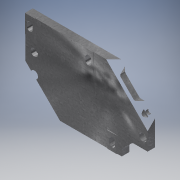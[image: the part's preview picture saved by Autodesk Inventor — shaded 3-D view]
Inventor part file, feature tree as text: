
AUTODESK INVENTOR PART (.ipt)
format: ipt  version: 2016 Beta3 (Build 200134000, 134) ContinuousBuild 0  size: 233,984 bytes
history: native  units: in
note: dims shown in document units (in); Inventor stores cm internally (conversion verified against a paired STEP export)
features: extrude x7, sketch x7, other x4, pattern_linear x3, fillet x1, hole x1
ambient origin geometry x8: Origin, YZ Plane, XZ Plane, XY Plane, X Axis, Y Axis, Z Axis, Center Point
bodies: Solid1 (feature_tree)
feature tree (23):
  extrude  "Extrusion1"  Depth=6.063in
  extrude  "Extrusion2"  Depth=2.3898in
  extrude  "Extrusion3"  TaperAngle=45.0deg  [1 undecoded]
  fillet  "Fillet1"  Radius=1.2087in
  extrude  "Extrusion4"  Depth=1.3602in
  extrude  "Extrusion5"  Depth=0.5906in TaperAngle=0.0deg
  other  "Work Point3"
  pattern_linear  "Rectangular Pattern1"  Count1=2  [1 undecoded]
  extrude  "Extrusion6"  Depth=0.0394in TaperAngle=0.0deg
  other  "Work Point1"
  pattern_linear  "Rectangular Pattern2"  Spacing1=0.0394in  [1 undecoded]
  hole  "Hole1"  [1 undecoded]
  pattern_linear  "Rectangular Pattern3"  Spacing1=0.7087in  [1 undecoded]
  sketch  "Sketch1"  dims[d0=9.7126in d1=6.063in]
  sketch  "Sketch2"  dims[d2=0.5906in d3=0.0in d4=2.3898in]
  sketch  "Sketch3"  dims[d5=4.1417in d6=45.0deg d7=1.2087in]
  sketch  "Sketch4"  dims[d8=0.5906in d9=0.0in d10=1.3602in]
  sketch  "Sketch5"  dims[d11=45.0deg d12=0.5906in d13=0.0in]
  sketch  "Sketch6"  dims[d14=0.25in]
  sketch  "Sketch7"  dims[d15=1.4567in d16=0.7874in d17=0.0394in d18=0.0in d21=0.0394in d22=0.0in d23=0.4724in d24=0.7087in d25=0.7874in d27=4.6457in d30=1.2835in d31=0.0394in d32=0.0in d33=0.7087in d34=0.4724in d36=0.0in d37=0.0394in d38=0.7874in d40=6.5354in d41=2.0591in d42=0.7087in d43=2.1476in d44=0.3465in d45=0.2362in d46=0.5906in d47=0.3543in d48=90.0deg d49=0.315in d50=0.8108in d51=0.7874in d53=1.5406in d54=0.7874in d56=8.6299in]
  other  "Work Point2"
  other  "Work Point4"
  extrude  "Extrusion7"  Depth=0.7874in
note: 5 required parameter values undecoded (feature->parameter linkage not recoverable at this tier; creation-order binding heuristic only, values carry confidence <= 0.55)
